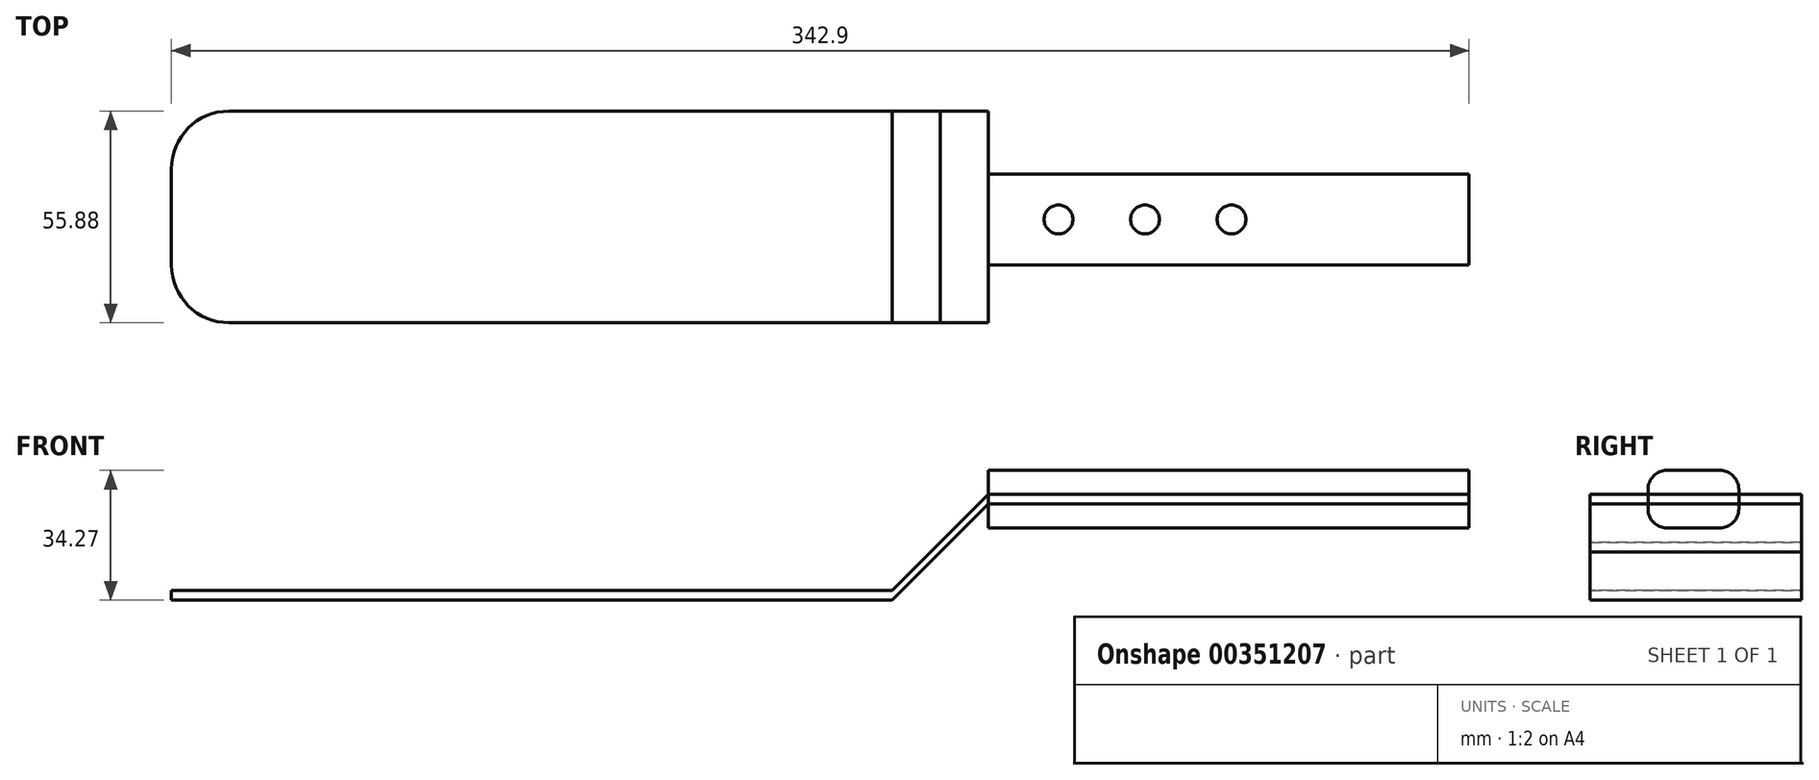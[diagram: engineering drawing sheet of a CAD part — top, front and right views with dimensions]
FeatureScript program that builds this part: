
annotation { "Feature Type Name" : "Feature", "Feature Type Description" : "" }
export const myFeature = defineFeature(function(context is Context, id is Id, definition is map)
    precondition{}
    {
        {
            var Q0;
            Q0=qCreatedBy(makeId("Top.planeOp"),FACE);
            var sketch = newSketch(context, id + "F0", { "sketchPlane" : qUnion([Q0])});
            skLineSegment(sketch, "E0.bottom", {"start": v(-76.04, 33.2) * mm, "end": v(114.46, 33.2) * mm});
            skLineSegment(sketch, "E0.top", {"start": v(-76.04, -22.68) * mm, "end": v(114.46, -22.68) * mm});
            skLineSegment(sketch, "E0.left", {"start": v(-76.04, 33.2) * mm, "end": v(-76.04, -22.68) * mm});
            skLineSegment(sketch, "E0.right", {"start": v(114.46, 33.2) * mm, "end": v(114.46, -22.68) * mm});
            skSolve(sketch);
        }
        {
            var Q0;
            Q0 = qSketchRegion(id + "F0", true);
            extrude(context, id + "F1", {"entities" : qUnion([Q0]), "depth" : 2.54 * mm});
        }
        {
            var Q0;
            Q0=makeQuery(id+"F1.opExtrude","SWEPT_FACE",FACE,{"disambiguationData":[OSD([sQuery(id+"F0.wireOp",EDGE,"E0.right")])]});
            var sketch = newSketch(context, id + "F2", { "sketchPlane" : qUnion([Q0])});
            skLineSegment(sketch, "E1.bottom", {"start": v(-22.68, 2.54) * mm, "end": v(33.2, 2.54) * mm});
            skLineSegment(sketch, "E1.top", {"start": v(-22.68, 0) * mm, "end": v(33.2, 0) * mm});
            skLineSegment(sketch, "E1.left", {"start": v(-22.68, 2.54) * mm, "end": v(-22.68, 0) * mm});
            skLineSegment(sketch, "E1.right", {"start": v(33.2, 2.54) * mm, "end": v(33.2, 0) * mm});
            skSolve(sketch);
        }
        {
            var Q0;
            Q0 = qSketchRegion(id + "F2", true);
            extrude(context, id + "F3", {"entities" : qUnion([Q0]), "depth" : 12.7 * mm});
        }
        {
            var Q0;
            Q0=makeQuery(id+"F3.opExtrude","SWEPT_FACE",FACE,{"disambiguationData":[OSD([sQuery(id+"F2.wireOp",EDGE,"E1.bottom")])]});
            var sketch = newSketch(context, id + "F4", { "sketchPlane" : qUnion([Q0])});
            skLineSegment(sketch, "E2.bottom", {"start": v(114.46, 33.2) * mm, "end": v(127.16, 33.2) * mm});
            skLineSegment(sketch, "E2.top", {"start": v(114.46, -22.68) * mm, "end": v(127.16, -22.68) * mm});
            skLineSegment(sketch, "E2.left", {"start": v(114.46, 33.2) * mm, "end": v(114.46, -22.68) * mm});
            skLineSegment(sketch, "E2.right", {"start": v(127.16, 33.2) * mm, "end": v(127.16, -22.68) * mm});
            skSolve(sketch);
        }
        {
            var Q0;
            Q0 = qSketchRegion(id + "F4", true);
            extrude(context, id + "F5", {"entities" : qUnion([Q0]), "operationType" : NewBodyOperationType.ADD, "depth" : 12.7 * mm});
        }
        {
            var Q0;
            Q0=makeQuery(id+"F5.boolean.opBoolean","MERGE",FACE,{"derivedFrom":[makeQuery(id+"F3.opExtrude","CAP_FACE",FACE,{"disambiguationData":[OSD([sQuery(id+"F2.wireOp",EDGE,"E1.bottom"),sQuery(id+"F2.wireOp",EDGE,"E1.top"),sQuery(id+"F2.wireOp",EDGE,"E1.left"),sQuery(id+"F2.wireOp",EDGE,"E1.right")])],"isStart":false}),makeQuery(id+"F5.opExtrude","SWEPT_FACE",FACE,{"disambiguationData":[OSD([sQuery(id+"F4.wireOp",EDGE,"E2.right")])]})]});
            var sketch = newSketch(context, id + "F6", { "sketchPlane" : qUnion([Q0])});
            skLineSegment(sketch, "E3.bottom", {"start": v(-22.68, 15.24) * mm, "end": v(33.2, 15.24) * mm});
            skLineSegment(sketch, "E3.top", {"start": v(-22.68, 12.7) * mm, "end": v(33.2, 12.7) * mm});
            skLineSegment(sketch, "E3.left", {"start": v(-22.68, 15.24) * mm, "end": v(-22.68, 12.7) * mm});
            skLineSegment(sketch, "E3.right", {"start": v(33.2, 15.24) * mm, "end": v(33.2, 12.7) * mm});
            skSolve(sketch);
        }
        {
            var Q0;
            Q0 = qSketchRegion(id + "F6", true);
            extrude(context, id + "F7", {"entities" : qUnion([Q0]), "operationType" : NewBodyOperationType.ADD, "depth" : 12.7 * mm});
        }
        {
            var Q0;
            Q0=makeQuery(id+"F7.boolean.opBoolean","MERGE",FACE,{"derivedFrom":[makeQuery(id+"F5.opExtrude","CAP_FACE",FACE,{"disambiguationData":[OSD([sQuery(id+"F4.wireOp",EDGE,"E2.bottom"),sQuery(id+"F4.wireOp",EDGE,"E2.top"),sQuery(id+"F4.wireOp",EDGE,"E2.left"),sQuery(id+"F4.wireOp",EDGE,"E2.right")])],"isStart":false}),makeQuery(id+"F7.opExtrude","SWEPT_FACE",FACE,{"disambiguationData":[OSD([sQuery(id+"F6.wireOp",EDGE,"E3.bottom")])]})]});
            var sketch = newSketch(context, id + "F8", { "sketchPlane" : qUnion([Q0])});
            skLineSegment(sketch, "E4.bottom", {"start": v(127.16, -22.68) * mm, "end": v(139.86, -22.68) * mm});
            skLineSegment(sketch, "E4.top", {"start": v(127.16, 33.2) * mm, "end": v(139.86, 33.2) * mm});
            skLineSegment(sketch, "E4.left", {"start": v(127.16, -22.68) * mm, "end": v(127.16, 33.2) * mm});
            skLineSegment(sketch, "E4.right", {"start": v(139.86, -22.68) * mm, "end": v(139.86, 33.2) * mm});
            skSolve(sketch);
        }
        {
            var Q0;
            Q0 = qSketchRegion(id + "F8", true);
            extrude(context, id + "F9", {"entities" : qUnion([Q0]), "operationType" : NewBodyOperationType.ADD, "depth" : 12.7 * mm});
        }
        {
            var Q0;
            Q0=makeQuery(id+"F9.opExtrude","CAP_EDGE",EDGE,{"disambiguationData":[OSD([sQuery(id+"F8.wireOp",EDGE,"E4.left")])],"isStart":false});
            var Q1;
            Q1=makeQuery(id+"F5.opExtrude","CAP_EDGE",EDGE,{"disambiguationData":[OSD([sQuery(id+"F4.wireOp",EDGE,"E2.left")])],"isStart":false});
            var Q2;
            Q2=makeQuery(id+"F7.opExtrude","CAP_EDGE",EDGE,{"disambiguationData":[OSD([sQuery(id+"F6.wireOp",EDGE,"E3.top")])],"isStart":false});
            var Q3;
            Q3=makeQuery(id+"F3.opExtrude","CAP_EDGE",EDGE,{"disambiguationData":[OSD([sQuery(id+"F2.wireOp",EDGE,"E1.top")])],"isStart":false});
            chamfer(context, id + "F10", {"entities" : qUnion([Q0, Q1, Q2, Q3]), "width" : 12.68 * mm, "tangentPropagation" : true});
        }
        {
            var Q0;
            Q0=makeQuery(id+"F10.opChamfer","BLEND_FACE",FACE,{"disambiguationData":[OSD([sQuery(id+"F8.wireOp",EDGE,"E4.left")])]});
            var sketch = newSketch(context, id + "F11", { "sketchPlane" : qUnion([Q0])});
            skLineSegment(sketch, "E5", {"start": v(82.94, 33.2) * mm, "end": v(118.64, 16.6) * mm});
            skLineSegment(sketch, "E6", {"start": v(82.8, -22.68) * mm, "end": v(118.64, -6.6) * mm});
            skLineSegment(sketch, "E7", {"start": v(118.64, -6.6) * mm, "end": v(118.64, -22.68) * mm});
            skLineSegment(sketch, "E8", {"start": v(118.64, -22.68) * mm, "end": v(82.8, -22.68) * mm});
            skLineSegment(sketch, "E9", {"start": v(118.64, 16.6) * mm, "end": v(118.64, 33.2) * mm});
            skLineSegment(sketch, "E10", {"start": v(118.64, 33.2) * mm, "end": v(82.94, 33.2) * mm});
            skSolve(sketch);
        }
        {
            var Q0;
            Q0 = qSketchRegion(id + "F11", true);
            extrude(context, id + "F12", {"entities" : qUnion([Q0]), "operationType" : NewBodyOperationType.REMOVE, "oppositeDirection" : true, "depth" : 25.4 * mm});
        }
        {
            var Q0;
            Q0=makeQuery(id+"F10.opChamfer","BLEND_FACE",FACE,{"disambiguationData":[OSD([sQuery(id+"F8.wireOp",EDGE,"E4.left")])]});
            var sketch = newSketch(context, id + "F13", { "sketchPlane" : qUnion([Q0])});
            skLineSegment(sketch, "E11", {"start": v(118.64, 16.6) * mm, "end": v(116.2, 21.23) * mm});
            skLineSegment(sketch, "E12", {"start": v(116.2, 21.23) * mm, "end": v(118.64, 36.18) * mm});
            skLineSegment(sketch, "E13", {"start": v(118.64, 36.18) * mm, "end": v(122.38, 27.36) * mm});
            skLineSegment(sketch, "E14", {"start": v(122.38, 27.36) * mm, "end": v(121.21, 14.95) * mm});
            skLineSegment(sketch, "E15", {"start": v(121.21, 14.95) * mm, "end": v(118.64, 16.6) * mm});
            skLineSegment(sketch, "E16", {"start": v(118.64, -6.6) * mm, "end": v(120.5, -7.49) * mm});
            skLineSegment(sketch, "E17", {"start": v(120.5, -7.49) * mm, "end": v(120.5, -19.79) * mm});
            skLineSegment(sketch, "E18", {"start": v(120.5, -19.79) * mm, "end": v(117.97, -25.1) * mm});
            skLineSegment(sketch, "E19", {"start": v(117.97, -25.1) * mm, "end": v(116.05, -18.36) * mm});
            skLineSegment(sketch, "E20", {"start": v(116.05, -18.36) * mm, "end": v(117, -8.28) * mm});
            skLineSegment(sketch, "E21", {"start": v(117, -8.28) * mm, "end": v(118.64, -6.6) * mm});
            skSolve(sketch);
        }
        {
            var Q0;
            Q0 = qSketchRegion(id + "F13", true);
            extrude(context, id + "F14", {"entities" : qUnion([Q0]), "operationType" : NewBodyOperationType.REMOVE, "oppositeDirection" : true, "depth" : 25.4 * mm});
        }
        {
            var Q0;
            Q0=makeQuery(id+"F9.boolean.opBoolean","MERGE",FACE,{"derivedFrom":[makeQuery(id+"F7.opExtrude","CAP_FACE",FACE,{"disambiguationData":[OSD([sQuery(id+"F6.wireOp",EDGE,"E3.bottom"),sQuery(id+"F6.wireOp",EDGE,"E3.top"),sQuery(id+"F6.wireOp",EDGE,"E3.left"),sQuery(id+"F6.wireOp",EDGE,"E3.right")])],"isStart":false}),makeQuery(id+"F9.opExtrude","SWEPT_FACE",FACE,{"disambiguationData":[OSD([sQuery(id+"F8.wireOp",EDGE,"E4.right")])]})]});
            var sketch = newSketch(context, id + "F15", { "sketchPlane" : qUnion([Q0])});
            skLineSegment(sketch, "E22.bottom", {"start": v(-7.4, 25.37) * mm, "end": v(16.6, 25.37) * mm});
            skLineSegment(sketch, "E22.top", {"start": v(-7.4, 27.92) * mm, "end": v(16.6, 27.92) * mm});
            skLineSegment(sketch, "E22.left", {"start": v(-7.4, 25.37) * mm, "end": v(-7.4, 27.92) * mm});
            skLineSegment(sketch, "E22.right", {"start": v(16.6, 25.37) * mm, "end": v(16.6, 27.92) * mm});
            skSolve(sketch);
        }
        {
            var Q0;
            Q0 = qSketchRegion(id + "F15", true);
            extrude(context, id + "F16", {"entities" : qUnion([Q0]), "depth" : 127 * mm});
        }
        {
            var Q0;
            Q0=makeQuery(id+"F16.opExtrude","SWEPT_FACE",FACE,{"disambiguationData":[OSD([sQuery(id+"F15.wireOp",EDGE,"E22.top")])]});
            var sketch = newSketch(context, id + "F17", { "sketchPlane" : qUnion([Q0])});
            skLineSegment(sketch, "E23.bottom", {"start": v(139.86, 16.6) * mm, "end": v(266.86, 16.6) * mm});
            skLineSegment(sketch, "E23.top", {"start": v(139.86, -7.4) * mm, "end": v(266.86, -7.4) * mm});
            skLineSegment(sketch, "E23.left", {"start": v(139.86, 16.6) * mm, "end": v(139.86, -7.4) * mm});
            skLineSegment(sketch, "E23.right", {"start": v(266.86, 16.6) * mm, "end": v(266.86, -7.4) * mm});
            skSolve(sketch);
        }
        {
            var Q0;
            Q0 = qSketchRegion(id + "F17", true);
            extrude(context, id + "F18", {"entities" : qUnion([Q0]), "depth" : 6.35 * mm});
        }
        {
            var Q0;
            Q0=makeQuery(id+"F16.opExtrude","SWEPT_FACE",FACE,{"disambiguationData":[OSD([sQuery(id+"F15.wireOp",EDGE,"E22.bottom")])]});
            var sketch = newSketch(context, id + "F19", { "sketchPlane" : qUnion([Q0])});
            skLineSegment(sketch, "E24.bottom", {"start": v(139.86, 7.4) * mm, "end": v(266.86, 7.4) * mm});
            skLineSegment(sketch, "E24.top", {"start": v(139.86, -16.6) * mm, "end": v(266.86, -16.6) * mm});
            skLineSegment(sketch, "E24.left", {"start": v(139.86, 7.4) * mm, "end": v(139.86, -16.6) * mm});
            skLineSegment(sketch, "E24.right", {"start": v(266.86, 7.4) * mm, "end": v(266.86, -16.6) * mm});
            skSolve(sketch);
        }
        {
            var Q0;
            Q0 = qSketchRegion(id + "F19", true);
            extrude(context, id + "F20", {"entities" : qUnion([Q0]), "depth" : 6.35 * mm});
        }
        {
            var Q0;
            Q0=makeQuery(id+"F1.opExtrude","SWEPT_EDGE",EDGE,{"disambiguationData":[OSD([sQuery(id+"F0.wireOp",EDGE,"E0.bottom"),sQuery(id+"F0.wireOp",EDGE,"E0.left")])]});
            var Q1;
            Q1=makeQuery(id+"F1.opExtrude","SWEPT_EDGE",EDGE,{"disambiguationData":[OSD([sQuery(id+"F0.wireOp",EDGE,"E0.top"),sQuery(id+"F0.wireOp",EDGE,"E0.left")])]});
            fillet(context, id + "F21", {"entities" : qUnion([Q0, Q1]), "radius" : 15.24 * mm, "tangentPropagation" : true, "allowEdgeOverflow" : false});
        }
        {
            var Q0;
            Q0=makeQuery(id+"F18.opExtrude","CAP_EDGE",EDGE,{"disambiguationData":[OSD([sQuery(id+"F17.wireOp",EDGE,"E23.top")])],"isStart":false});
            var Q1;
            Q1=makeQuery(id+"F18.opExtrude","CAP_EDGE",EDGE,{"disambiguationData":[OSD([sQuery(id+"F17.wireOp",EDGE,"E23.bottom")])],"isStart":false});
            var Q2;
            Q2=makeQuery(id+"F20.opExtrude","CAP_EDGE",EDGE,{"disambiguationData":[OSD([sQuery(id+"F19.wireOp",EDGE,"E24.bottom")])],"isStart":false});
            var Q3;
            Q3=makeQuery(id+"F20.opExtrude","CAP_EDGE",EDGE,{"disambiguationData":[OSD([sQuery(id+"F19.wireOp",EDGE,"E24.top")])],"isStart":false});
            fillet(context, id + "F22", {"entities" : qUnion([Q0, Q1, Q2, Q3]), "radius" : 5.08 * mm, "tangentPropagation" : true, "allowEdgeOverflow" : false});
        }
        {
            var Q0;
            Q0=makeQuery(id+"F18.opExtrude","CAP_FACE",FACE,{"disambiguationData":[OSD([sQuery(id+"F17.wireOp",EDGE,"E23.bottom"),sQuery(id+"F17.wireOp",EDGE,"E23.top"),sQuery(id+"F17.wireOp",EDGE,"E23.left"),sQuery(id+"F17.wireOp",EDGE,"E23.right")])],"isStart":false});
            var sketch = newSketch(context, id + "F23", { "sketchPlane" : qUnion([Q0])});
            skCircle(sketch, "E25", {"center": v(158.37, 4.6) * mm, "radius": 3.81 * mm});
            skPoint(sketch, "E25.centerSnap0", {"position": v(139.86, 4.6) * mm});
            skCircle(sketch, "E26", {"center": v(181.23, 4.6) * mm, "radius": 3.81 * mm});
            skCircle(sketch, "E27", {"center": v(204.09, 4.6) * mm, "radius": 3.81 * mm});
            skSolve(sketch);
        }
        {
            var Q0;
            Q0 = qSketchRegion(id + "F23", true);
            extrude(context, id + "F24", {"entities" : qUnion([Q0]), "depth" : 0 * mm});
        }
    });
